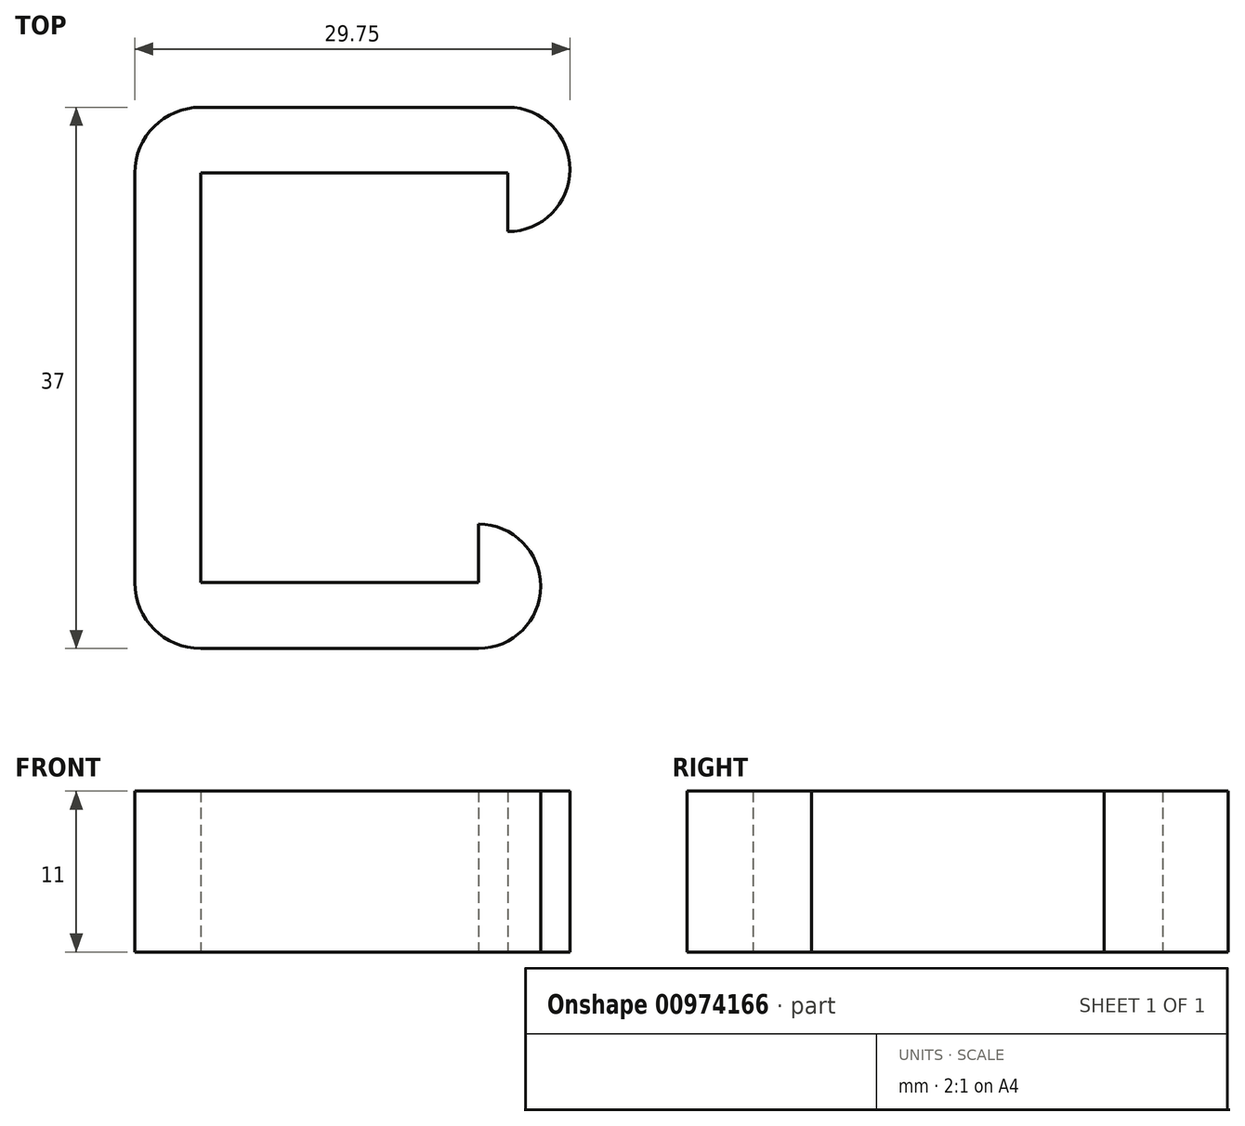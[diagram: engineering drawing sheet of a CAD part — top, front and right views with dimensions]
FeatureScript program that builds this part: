
annotation { "Feature Type Name" : "Feature", "Feature Type Description" : "" }
export const myFeature = defineFeature(function(context is Context, id is Id, definition is map)
    precondition{}
    {
        {
            var Q0;
            Q0=qCreatedBy(makeId("Top.planeOp"),FACE);
            var sketch = newSketch(context, id + "F0", { "sketchPlane" : qUnion([Q0])});
            skLineSegment(sketch, "E0", {"start": v(0, 0) * mm, "end": v(0, 28) * mm});
            skLineSegment(sketch, "E1", {"start": v(0, 0) * mm, "end": v(19, 0) * mm});
            skLineSegment(sketch, "E2", {"start": v(0, 28) * mm, "end": v(21, 28) * mm});
            skLineSegment(sketch, "E3", {"start": v(21, 28) * mm, "end": v(21, 24) * mm});
            skLineSegment(sketch, "E4", {"start": v(19, 0) * mm, "end": v(19, 4) * mm});
            skLineSegment(sketch, "E5.0", {"start": v(0, 32.5) * mm, "end": v(21, 32.5) * mm});
            skLineSegment(sketch, "E6.0", {"start": v(-4.5, 0) * mm, "end": v(-4.5, 28) * mm});
            skLineSegment(sketch, "E7.0", {"start": v(0, -4.5) * mm, "end": v(19, -4.5) * mm});
            skArc(sketch, "E8", {"start": v(-4.5, 0) * mm, "mid": v(-3.18, -3.18) * mm, "end": v(0, -4.5) * mm});
            skArc(sketch, "E9", {"start": v(0, 32.5) * mm, "mid": v(-3.18, 31.18) * mm, "end": v(-4.5, 28) * mm});
            skArc(sketch, "E10", {"start": v(21, 24) * mm, "mid": v(25.25, 28.25) * mm, "end": v(21, 32.5) * mm});
            skArc(sketch, "E11", {"start": v(19, -4.5) * mm, "mid": v(23.25, -0.25) * mm, "end": v(19, 4) * mm});
            skSolve(sketch);
        }
        {
            var Q0;
            Q0 = qSketchRegion(id + "F0", true);
            extrude(context, id + "F1", {"entities" : qUnion([Q0]), "depth" : 11 * mm, "offsetDistance" : 25 * mm});
        }
    });
